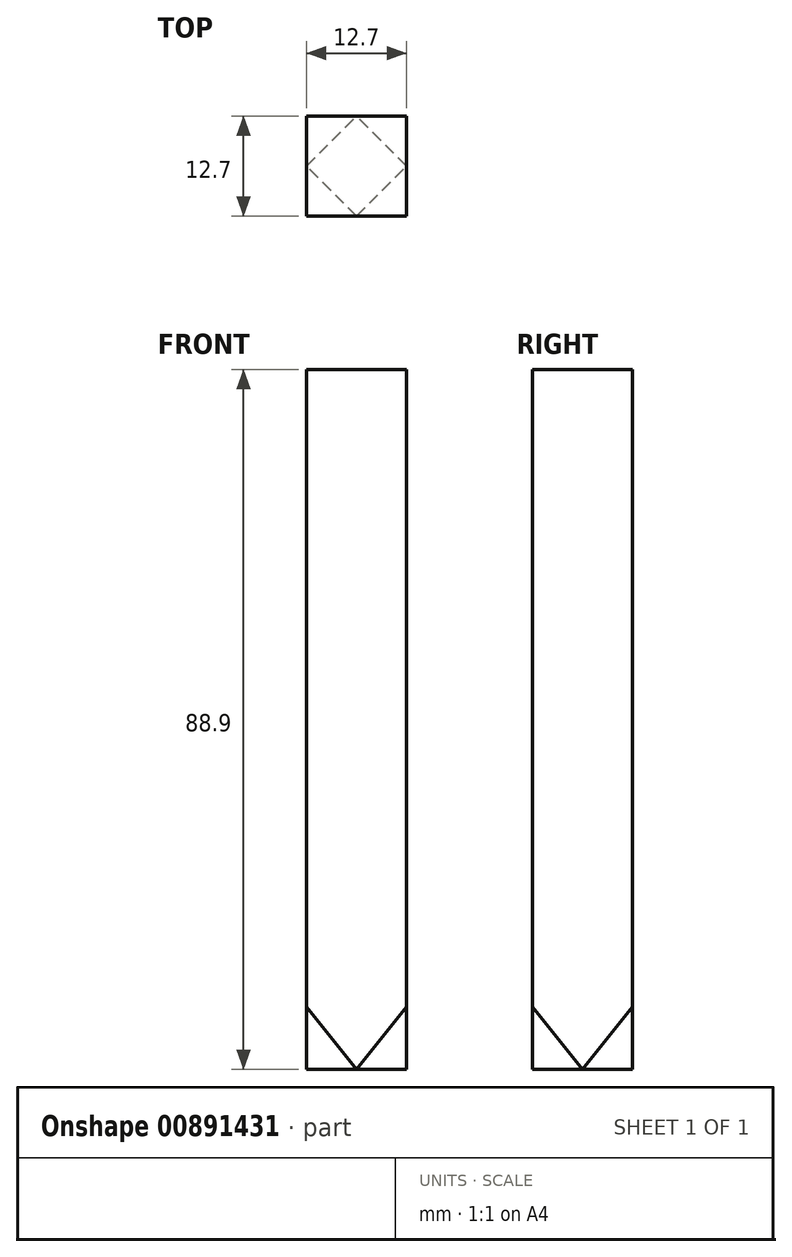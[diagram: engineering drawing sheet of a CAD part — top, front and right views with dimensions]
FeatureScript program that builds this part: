
annotation { "Feature Type Name" : "Feature", "Feature Type Description" : "" }
export const myFeature = defineFeature(function(context is Context, id is Id, definition is map)
    precondition{}
    {
        {
            var Q0;
            Q0=qCreatedBy(makeId("Top.planeOp"),FACE);
            var sketch = newSketch(context, id + "F0", { "sketchPlane" : qUnion([Q0])});
            skLineSegment(sketch, "E0.bottom", {"start": v(6.35, 6.35) * mm, "end": v(-6.35, 6.35) * mm});
            skLineSegment(sketch, "E0.top", {"start": v(6.35, -6.35) * mm, "end": v(-6.35, -6.35) * mm});
            skLineSegment(sketch, "E0.left", {"start": v(6.35, 6.35) * mm, "end": v(6.35, -6.35) * mm});
            skLineSegment(sketch, "E0.right", {"start": v(-6.35, 6.35) * mm, "end": v(-6.35, -6.35) * mm});
            skPoint(sketch, "E0.middle", {"position": v(0, 0) * mm});
            skSolve(sketch);
        }
        {
            var Q0;
            Q0=makeQuery(id+"F0.imprint","IMPRINT",FACE,{"disambiguationData":[TD([[makeQuery(id+"F0.imprint","IMPRINT",EDGE,{"derivedFrom":sQuery(id+"F0.wireOp",EDGE,"E0.bottom")}),1.0]])]});
            extrude(context, id + "F1", {"entities" : qUnion([Q0]), "oppositeDirection" : true, "depth" : 88.9 * mm, "offsetDistance" : 25.4 * mm});
        }
        {
            var Q0;
            Q0=makeQuery(id+"F1.opExtrude","SWEPT_FACE",FACE,{"disambiguationData":[OSD([sQuery(id+"F0.wireOp",EDGE,"E0.top")])]});
            var sketch = newSketch(context, id + "F2", { "sketchPlane" : qUnion([Q0])});
            skLineSegment(sketch, "E1.0", {"start": v(-6.35, -88.9) * mm, "end": v(-6.35, 0) * mm, "construction": true});
            skLineSegment(sketch, "E2.0", {"start": v(6.35, -88.9) * mm, "end": v(6.35, 0) * mm, "construction": true});
            skLineSegment(sketch, "E3.0", {"start": v(6.35, -88.9) * mm, "end": v(-6.35, -88.9) * mm, "construction": true});
            skPoint(sketch, "E4", {"position": v(0, -88.9) * mm});
            skPoint(sketch, "E5", {"position": v(6.35, -80.97) * mm});
            skPoint(sketch, "E6", {"position": v(-6.35, -80.97) * mm});
            skSolve(sketch);
        }
        {
            var Q0;
            Q0=makeQuery(id+"F1.opExtrude","SWEPT_FACE",FACE,{"disambiguationData":[OSD([sQuery(id+"F0.wireOp",EDGE,"E0.left")])]});
            var sketch = newSketch(context, id + "F3", { "sketchPlane" : qUnion([Q0])});
            skLineSegment(sketch, "E7.0", {"start": v(6.35, -88.9) * mm, "end": v(-6.35, -88.9) * mm, "construction": true});
            skLineSegment(sketch, "E8.0", {"start": v(-6.35, -88.9) * mm, "end": v(-6.35, 0) * mm, "construction": true});
            skLineSegment(sketch, "E9.0", {"start": v(6.35, -88.9) * mm, "end": v(6.35, 0) * mm, "construction": true});
            skPoint(sketch, "E10", {"position": v(0, -88.9) * mm});
            skPoint(sketch, "E11.0", {"position": v(-6.35, -80.97) * mm});
            skPoint(sketch, "E12", {"position": v(6.35, -80.97) * mm});
            skSolve(sketch);
        }
        {
            var Q0;
            Q0=makeQuery(id+"F1.opExtrude","SWEPT_FACE",FACE,{"disambiguationData":[OSD([sQuery(id+"F0.wireOp",EDGE,"E0.bottom")])]});
            var sketch = newSketch(context, id + "F4", { "sketchPlane" : qUnion([Q0])});
            skPoint(sketch, "E13.0", {"position": v(-6.35, -80.97) * mm});
            skPoint(sketch, "E14.0", {"position": v(0, -88.9) * mm});
            skPoint(sketch, "E15.0", {"position": v(6.35, -80.97) * mm});
            skSolve(sketch);
        }
        {
            var Q0;
            Q0=makeQuery(id+"F1.opExtrude","SWEPT_FACE",FACE,{"disambiguationData":[OSD([sQuery(id+"F0.wireOp",EDGE,"E0.right")])]});
            var sketch = newSketch(context, id + "F5", { "sketchPlane" : qUnion([Q0])});
            skPoint(sketch, "E16.0", {"position": v(-6.35, -80.97) * mm});
            skPoint(sketch, "E17.0", {"position": v(0, -88.9) * mm});
            skPoint(sketch, "E18.0", {"position": v(6.35, -80.97) * mm});
            skSolve(sketch);
        }
        {
            var Q0;
            Q0=sQuery(id+"F4.wireOp",VERTEX,"E15.0");
            var Q1;
            Q1=sQuery(id+"F5.wireOp",VERTEX,"E17.0");
            var Q2;
            Q2=sQuery(id+"F4.wireOp",VERTEX,"E14.0");
            cPlane(context, id + "F6", {"entities" : qUnion([Q0, Q1, Q2]), "cplaneType" : CPlaneType.THREE_POINT, "offset" : 25.4 * mm, "width" : 152.4 * mm, "height" : 152.4 * mm});
        }
        {
            var Q0;
            Q0=sQuery(id+"F5.wireOp",VERTEX,"E17.0");
            var Q1;
            Q1=sQuery(id+"F2.wireOp",VERTEX,"E6");
            var Q2;
            Q2=sQuery(id+"F2.wireOp",VERTEX,"E4");
            cPlane(context, id + "F7", {"entities" : qUnion([Q0, Q1, Q2]), "cplaneType" : CPlaneType.THREE_POINT, "offset" : 25.4 * mm, "width" : 152.4 * mm, "height" : 152.4 * mm});
        }
        {
            var Q0;
            Q0=sQuery(id+"F2.wireOp",VERTEX,"E5");
            var Q1;
            Q1=sQuery(id+"F2.wireOp",VERTEX,"E4");
            var Q2;
            Q2=sQuery(id+"F3.wireOp",VERTEX,"E10");
            cPlane(context, id + "F8", {"entities" : qUnion([Q0, Q1, Q2]), "cplaneType" : CPlaneType.THREE_POINT, "offset" : 25.4 * mm, "width" : 152.4 * mm, "height" : 152.4 * mm});
        }
        {
            var Q0;
            Q0=sQuery(id+"F3.wireOp",EDGE,"E7.0");
            cPoint(context, id + "F9", {"entities" : qUnion([Q0]), "parameter" : 0.5});
        }
        {
            var Q0;
            Q0 = qCreatedBy(id + "F9" ,VERTEX);
            var Q1;
            Q1=sQuery(id+"F4.wireOp",VERTEX,"E14.0");
            var Q2;
            Q2=sQuery(id+"F3.wireOp",VERTEX,"E12");
            cPlane(context, id + "F10", {"entities" : qUnion([Q0, Q1, Q2]), "cplaneType" : CPlaneType.THREE_POINT, "offset" : 25.4 * mm, "width" : 152.4 * mm, "height" : 152.4 * mm});
        }
        {
            var Q0;
            Q0=qCreatedBy(id+"F6.planeOp",FACE);
            var sketch = newSketch(context, id + "F11", { "sketchPlane" : qUnion([Q0])});
            skPoint(sketch, "E19.0", {"position": v(-29.18, -59.24) * mm});
            skPoint(sketch, "E20.0", {"position": v(-29.18, -69.4) * mm});
            skPoint(sketch, "E21.0", {"position": v(-37.24, -65.43) * mm});
            skLineSegment(sketch, "E22", {"start": v(-29.18, -59.24) * mm, "end": v(-29.18, -69.4) * mm});
            skLineSegment(sketch, "E23", {"start": v(-37.24, -65.43) * mm, "end": v(-29.18, -59.24) * mm});
            skLineSegment(sketch, "E24", {"start": v(-29.18, -69.4) * mm, "end": v(-37.24, -65.43) * mm});
            skSolve(sketch);
        }
        {
            var Q0;
            Q0=qCreatedBy(id+"F7.planeOp",FACE);
            var sketch = newSketch(context, id + "F12", { "sketchPlane" : qUnion([Q0])});
            skPoint(sketch, "E25.0", {"position": v(29.18, -59.24) * mm});
            skPoint(sketch, "E26.0", {"position": v(29.18, -69.4) * mm});
            skPoint(sketch, "E27.0", {"position": v(37.24, -65.43) * mm});
            skLineSegment(sketch, "E28", {"start": v(29.18, -59.24) * mm, "end": v(29.18, -69.4) * mm});
            skLineSegment(sketch, "E29", {"start": v(37.24, -65.43) * mm, "end": v(29.18, -69.4) * mm});
            skLineSegment(sketch, "E30", {"start": v(29.18, -59.24) * mm, "end": v(37.24, -65.43) * mm});
            skSolve(sketch);
        }
        {
            var Q0;
            Q0=qCreatedBy(id+"F8.planeOp",FACE);
            var sketch = newSketch(context, id + "F13", { "sketchPlane" : qUnion([Q0])});
            skPoint(sketch, "E31.0", {"position": v(29.18, -59.24) * mm});
            skPoint(sketch, "E32.0", {"position": v(29.18, -69.4) * mm});
            skPoint(sketch, "E33.0", {"position": v(37.24, -65.43) * mm});
            skLineSegment(sketch, "E34", {"start": v(29.18, -69.4) * mm, "end": v(29.18, -59.24) * mm});
            skLineSegment(sketch, "E35", {"start": v(37.24, -65.43) * mm, "end": v(29.18, -59.24) * mm});
            skLineSegment(sketch, "E36", {"start": v(37.24, -65.43) * mm, "end": v(29.18, -69.4) * mm});
            skSolve(sketch);
        }
        {
            var Q0;
            Q0=qCreatedBy(id+"F10.planeOp",FACE);
            var sketch = newSketch(context, id + "F14", { "sketchPlane" : qUnion([Q0])});
            skPoint(sketch, "E37.0", {"position": v(-29.18, -69.4) * mm});
            skPoint(sketch, "E38.0", {"position": v(-29.18, -59.24) * mm});
            skPoint(sketch, "E39.0", {"position": v(-37.24, -65.43) * mm});
            skLineSegment(sketch, "E40", {"start": v(-29.18, -59.24) * mm, "end": v(-37.24, -65.43) * mm});
            skLineSegment(sketch, "E41", {"start": v(-29.18, -69.4) * mm, "end": v(-29.18, -59.24) * mm});
            skLineSegment(sketch, "E42", {"start": v(-29.18, -69.4) * mm, "end": v(-37.24, -65.43) * mm});
            skSolve(sketch);
        }
        {
            var Q0;
            Q0 = qSketchRegion(id + "F11", true);
            extrude(context, id + "F15", {"entities" : qUnion([Q0]), "operationType" : NewBodyOperationType.REMOVE, "depth" : 25.4 * mm, "offsetDistance" : 25.4 * mm});
        }
        {
            var Q0;
            Q0 = qSketchRegion(id + "F12", true);
            extrude(context, id + "F16", {"entities" : qUnion([Q0]), "operationType" : NewBodyOperationType.REMOVE, "depth" : 25.4 * mm, "offsetDistance" : 25.4 * mm});
        }
        {
            var Q0;
            Q0 = qSketchRegion(id + "F13", true);
            extrude(context, id + "F17", {"entities" : qUnion([Q0]), "operationType" : NewBodyOperationType.REMOVE, "oppositeDirection" : true, "depth" : 25.4 * mm, "offsetDistance" : 25.4 * mm});
        }
        {
            var Q0;
            Q0 = qSketchRegion(id + "F14", true);
            extrude(context, id + "F18", {"entities" : qUnion([Q0]), "operationType" : NewBodyOperationType.REMOVE, "oppositeDirection" : true, "depth" : 25.4 * mm, "offsetDistance" : 25.4 * mm});
        }
    });
